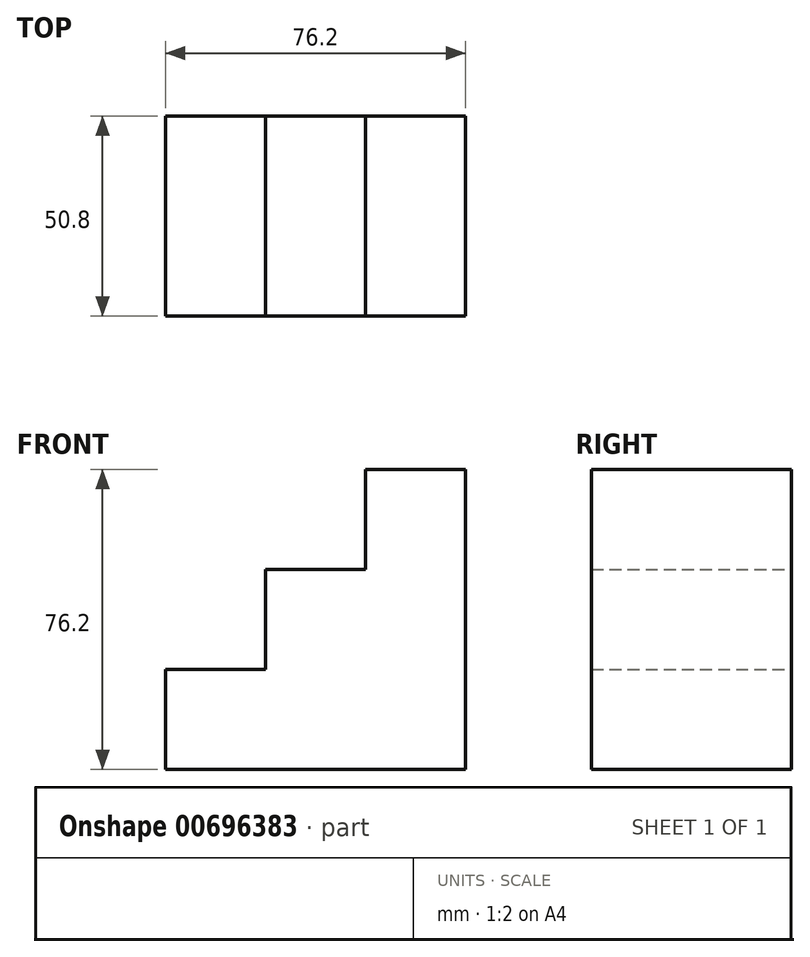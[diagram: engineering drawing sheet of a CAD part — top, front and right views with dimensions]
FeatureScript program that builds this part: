
annotation { "Feature Type Name" : "Feature", "Feature Type Description" : "" }
export const myFeature = defineFeature(function(context is Context, id is Id, definition is map)
    precondition{}
    {
        {
            var Q0;
            Q0=qCreatedBy(makeId("Front.planeOp"),FACE);
            var sketch = newSketch(context, id + "F0", { "sketchPlane" : qUnion([Q0])});
            skLineSegment(sketch, "E0.bottom", {"start": v(0, 0) * mm, "end": v(-76.2, 0) * mm});
            skLineSegment(sketch, "E0.top", {"start": v(0, 76.2) * mm, "end": v(-25.4, 76.2) * mm});
            skLineSegment(sketch, "E0.left", {"start": v(0, 0) * mm, "end": v(0, 76.2) * mm});
            skLineSegment(sketch, "E0.right", {"start": v(-76.2, 0) * mm, "end": v(-76.2, 25.4) * mm});
            skLineSegment(sketch, "E1", {"start": v(-76.2, 25.4) * mm, "end": v(-50.8, 25.4) * mm});
            skLineSegment(sketch, "E2", {"start": v(-50.8, 25.4) * mm, "end": v(-50.8, 50.8) * mm});
            skLineSegment(sketch, "E3", {"start": v(-50.8, 50.8) * mm, "end": v(-25.4, 50.8) * mm});
            skLineSegment(sketch, "E4", {"start": v(-25.4, 50.8) * mm, "end": v(-25.4, 76.2) * mm});
            skSolve(sketch);
        }
        {
            var Q0;
            Q0 = qSketchRegion(id + "F0", true);
            extrude(context, id + "F1", {"entities" : qUnion([Q0]), "depth" : 50.8 * mm, "offsetDistance" : 25.4 * mm});
        }
    });
